# Revit family: HL_RU_Roof drain_HL64F-B-221103
name_source: partatom
category: Sanitärinstallationen
units: mm (PartAtom-declared; Revit-internal decimal feet)

## family parameters
Arbeitsebenenbasiert = Nein
Beim Laden mit Abzugskörper schneiden = Nein
Bemaßung runder Anschluss = Durchmesser verwenden
Gemeinsam genutzt = Nein
Immer vertikal = Ja
OmniClass-Nummer = 23.70.50.21.24.14
OmniClass-Titel = Deck Waste Water Drains
Raumberechnungspunkt = Ja
Teiletyp = Normal

## types (2) — shared parameters
Abwasserrohrverbindung = Ja
Beschreibung = Кровельные воронки
HW-Verbindung = Nein
Hersteller = HL Hutterer & Lechner GmbH
KW-Verbindung = Nein
Lüftungsverbindung = Nein
URL = http://www.hutterer-lechner.com
МАТЕРИАЛ = PP
РЕШЁТКА = Laubfangkorb d 145 mm
zero-valued in all types: Vorgabe-Ansicht

## per-type parameters (varying)
| type | Bauelement | EAN | Modell | Typenkommentare | ВЕС | НОМИНАЛЬНЫЙ ДИАМЕТР | ПРОИЗВОДИТЕЛЬНОСТЬ | РАЗМЕР |
| HL_Кровельная воронка_HL64F_1 | HL64F_1 | 9003076031702 | HL64F_1 | HL64F/1 Кровельная воронка DN110, горизонтальный выпуск, с ПП_фланцем, | 0,872 [kg] | 100 mm | 7,8 l/s | DN10 |
| HL_Кровельная воронка_HL64F_7 | HL64F_7 | 9003076031689 | HL64F_7 | HL64F/7 Кровельная воронка DN75, горизонтальный выпуск, с ПП_фланцем, | 0,761 [kg] | 75 mm | 6,9l/s | DN75 |

## geometry (parser evidence)
native form markers: Sweep x12
no freeform markers — native parametric forms only
